# Revit family: 712-0220-001-DN50
name_source: partatom
category: Pipe Fittings
units: mm (PartAtom-declared; Revit-internal decimal feet)

## family parameters
Always vertical = Yes
Cut with Voids When Loaded = No
Part Type = Elbow
Round Connector Dimension = Use Diameter
Shared = No
Work Plane-Based = No

## types (1)
- DN050_PN10/16
    A = 22.50°
    Body_wallthickness = 65 mm  [stored 0.213255 ft]
    DN050_ PN10/16 = Yes
    DN050_PN10/16 = 712-0050-02-201
    Description_ = AVK FLANGED BEND 22.5° W/LOOSE FLANGES, PN 10/16
    FOD = 83 mm
    Flange_thickness = 17 mm
    ID(Radius) = 25 mm  [stored 0.082021 ft]
    L = 104 mm
    L_Ref = 50 mm  [stored 0.164042 ft]
    Nominal Diameter(DN) = 50 mm  [stored 0.164042 ft]
    RF_Thick = 3 mm  [stored 0.00984252 ft]
    Rf_Dia = 50 mm  [stored 0.164042 ft]
    URL product pages = https://www.avkvalves.com

note: [stored X ft] marks values corroborated as IEEE doubles in the binary element streams (Revit-internal decimal feet)

## geometry (parser evidence)
native form markers: Sweep x5
no freeform markers — native parametric forms only
